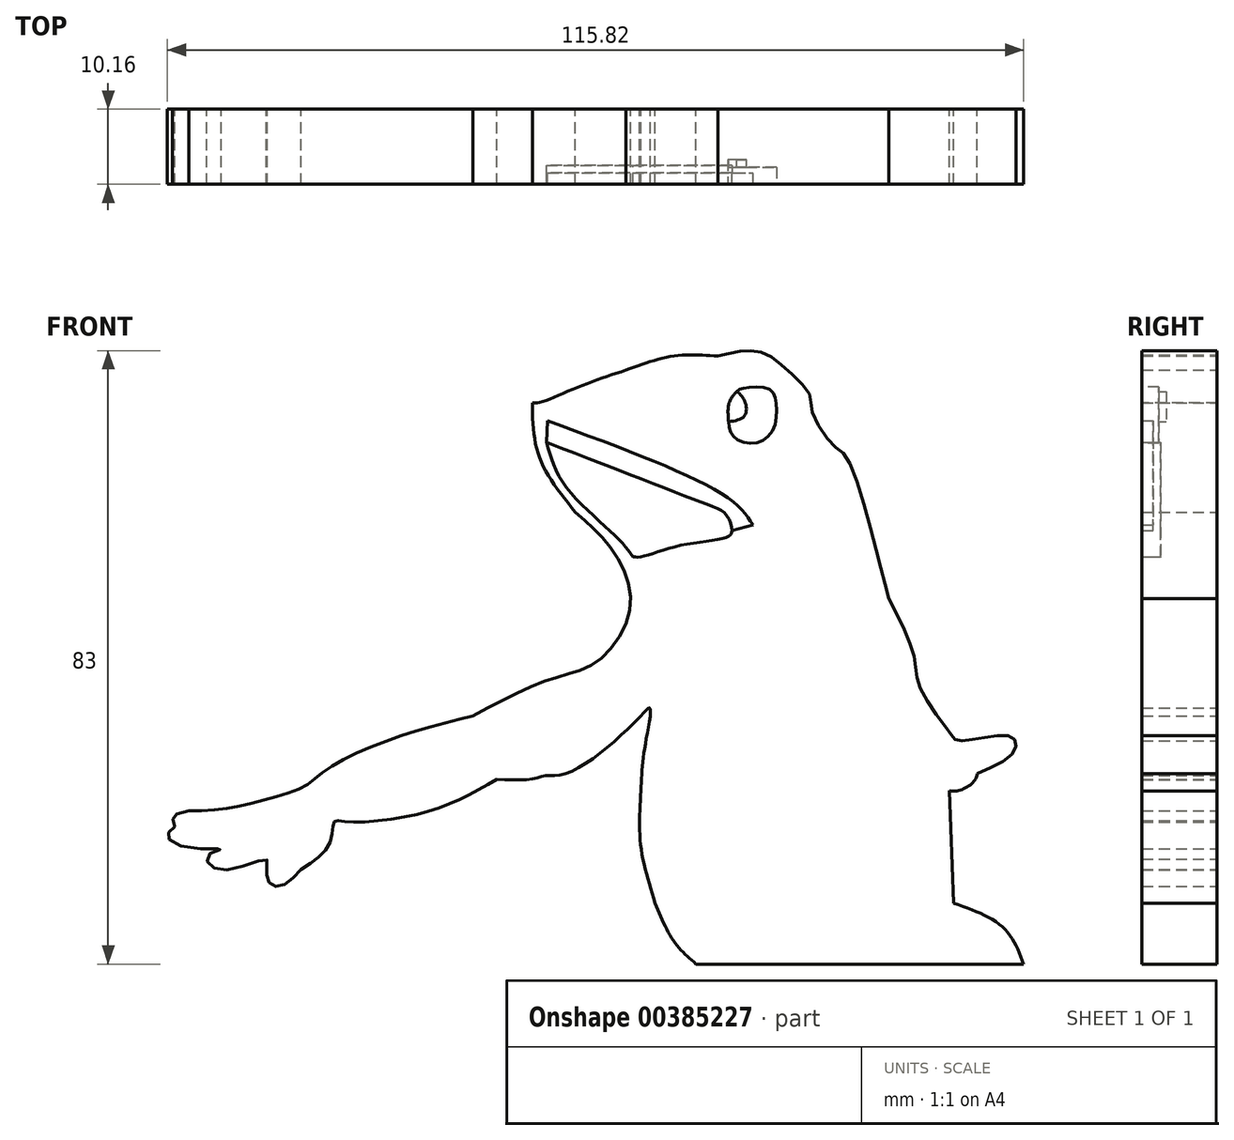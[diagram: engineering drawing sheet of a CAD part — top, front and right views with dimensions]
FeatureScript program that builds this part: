
annotation { "Feature Type Name" : "Feature", "Feature Type Description" : "" }
export const myFeature = defineFeature(function(context is Context, id is Id, definition is map)
    precondition{}
    {
        {
            var Q0;
            Q0=qCreatedBy(makeId("Front.planeOp"),FACE);
            var sketch = newSketch(context, id + "F0", { "sketchPlane" : qUnion([Q0])});
            skFitSpline(sketch, "E0", {"points": [v(-7.4, 26.5) * mm, v(-2.35, 21.3) * mm, v(0, 13.64) * mm, v(-4.52, 6.27) * mm, v(-11.02, 3.82) * mm, v(-21.28, -1.1) * mm], "startDerivative": vector(29, -25.3) * mm, "endDerivative": vector(-46.1, -24.95) * mm});
            skFitSpline(sketch, "E1", {"points": [v(-21.28, -1.1) * mm, v(-28.33, -2.93) * mm, v(-36.55, -5.9) * mm, v(-41.81, -8.85) * mm, v(-44.2, -10.67) * mm, v(-48.7, -12.2) * mm, v(-54.15, -13.54) * mm, v(-59.7, -13.92) * mm], "startDerivative": vector(-42.57, -10.25) * mm, "endDerivative": vector(-39.63, -0.97) * mm});
            skFitSpline(sketch, "E2", {"points": [v(-59.7, -13.92) * mm, v(-61.9, -14.78) * mm, v(-61.6, -16.03) * mm, v(-62.56, -17.08) * mm, v(-60.55, -18.7) * mm, v(-55.3, -19.09) * mm, v(-57.01, -19.85) * mm, v(-56.82, -21.28) * mm, v(-53.29, -21.67) * mm, v(-49.17, -20.52) * mm, v(-49.17, -21.57) * mm, v(-49.08, -23) * mm, v(-48.31, -24.06) * mm, v(-46.6, -23.77) * mm, v(-44.49, -21.86) * mm], "startDerivative": vector(-42.46, -7.69) * mm, "endDerivative": vector(24.54, 27.2) * mm});
            skFitSpline(sketch, "E3", {"points": [v(-44.49, -21.86) * mm, v(-40.57, -18.13) * mm, v(-40, -15.36) * mm, v(-38.66, -15.36) * mm, v(-30.72, -14.78) * mm, v(-23.55, -12.58) * mm, v(-18, -9.62) * mm], "startDerivative": vector(28.5, 18.95) * mm, "endDerivative": vector(28.54, 16.57) * mm});
            skFitSpline(sketch, "E4", {"points": [v(-18, -9.62) * mm, v(-13.32, -9.62) * mm, v(-11.37, -9.15) * mm, v(-9.27, -9.02) * mm, v(-4.35, -6.33) * mm, v(1.45, -1.1) * mm], "startDerivative": vector(24.57, -1.44) * mm, "endDerivative": vector(20.58, 20.22) * mm});
            skFitSpline(sketch, "E5", {"points": [v(1.45, -1.1) * mm, v(2.66, 0) * mm, v(2.27, -3.7) * mm, v(1.66, -7.93) * mm, v(1.45, -11.2) * mm], "startDerivative": vector(8.38, 10.25) * mm, "endDerivative": vector(-0.61, -12.7) * mm});
            skFitSpline(sketch, "E6", {"points": [v(1.45, -11.2) * mm, v(1.45, -18.68) * mm, v(3.4, -26.4) * mm], "startDerivative": vector(-0.94, -15.2) * mm, "endDerivative": vector(4.8, -15.2) * mm});
            skFitSpline(sketch, "E7", {"points": [v(3.4, -26.4) * mm, v(1.45, -30.92) * mm, v(-1.79, -34.64) * mm], "startDerivative": vector(-3.25, -9.45) * mm, "endDerivative": vector(-7.12, -7.03) * mm});
            skFitSpline(sketch, "E8", {"points": [v(3.4, -26.4) * mm, v(5.93, -31.58) * mm, v(8.9, -34.64) * mm], "startDerivative": vector(4.25, -10.45) * mm, "endDerivative": vector(6.84, -5.9) * mm});
            skFitSpline(sketch, "E9", {"points": [v(43.2, -11.2) * mm, v(43.75, -26.4) * mm], "startDerivative": vector(0.55, -15.2) * mm, "endDerivative": vector(0.55, -15.2) * mm});
            skFitSpline(sketch, "E10", {"points": [v(43.75, -26.4) * mm, v(50.47, -29.7) * mm, v(53.23, -34.64) * mm], "startDerivative": vector(14.34, -5) * mm, "endDerivative": vector(4.4, -11.64) * mm});
            skFitSpline(sketch, "E11", {"points": [v(43.2, -11.2) * mm, v(44.29, -11.2) * mm, v(46.35, -10.11) * mm, v(46.95, -8.91) * mm], "startDerivative": vector(3.44, -0.5) * mm, "endDerivative": vector(1.11, 3.96) * mm});
            skFitSpline(sketch, "E12", {"points": [v(46.95, -8.91) * mm, v(51.88, -5.91) * mm, v(51.88, -4.1) * mm, v(48.18, -3.93) * mm, v(44.21, -4.38) * mm, v(43.2, -3.3) * mm, v(39.16, 2.84) * mm, v(38.44, 6.8) * mm, v(35.01, 14.83) * mm], "startDerivative": vector(43.1, 18.83) * mm, "endDerivative": vector(-25.13, 49.69) * mm});
            skFitSpline(sketch, "E13", {"points": [v(23.2, 15.2) * mm, v(23.28, 3.65) * mm], "startDerivative": vector(0.1, -11.55) * mm, "endDerivative": vector(0.1, -11.55) * mm});
            skFitSpline(sketch, "E14", {"points": [v(23.28, 3.65) * mm, v(23.73, 2.55) * mm, v(25.33, 1.66) * mm], "startDerivative": vector(0.57, -2.65) * mm, "endDerivative": vector(3.42, -1.38) * mm});
            skFitSpline(sketch, "E15", {"points": [v(25.33, 1.66) * mm, v(25.12, 2.74) * mm], "startDerivative": vector(-0.21, 1.09) * mm, "endDerivative": vector(-0.21, 1.09) * mm});
            skFitSpline(sketch, "E16", {"points": [v(25.33, 1.66) * mm, v(26.38, -1.04) * mm, v(30.42, -5.41) * mm, v(31.88, -6.62) * mm], "startDerivative": vector(1.83, -8.12) * mm, "endDerivative": vector(4.88, -3.75) * mm});
            skFitSpline(sketch, "E17", {"points": [v(31.88, -6.62) * mm, v(32.96, -7.9) * mm, v(34.1, -9.43) * mm], "startDerivative": vector(2.21, -2.6) * mm, "endDerivative": vector(2.23, -3.01) * mm});
            skFitSpline(sketch, "E18", {"points": [v(33.45, -8.55) * mm, v(33.4, -10.6) * mm, v(32.88, -12.98) * mm, v(31.48, -16.79) * mm, v(30.7, -19.45) * mm], "startDerivative": vector(0.1, -9.6) * mm, "endDerivative": vector(-2.6, -10.02) * mm});
            skFitSpline(sketch, "E19", {"points": [v(30.7, -19.45) * mm, v(30.7, -20.82) * mm, v(32.66, -19.45) * mm, v(34.73, -14.35) * mm], "startDerivative": vector(-1.55, -8) * mm, "endDerivative": vector(3.26, 12.16) * mm});
            skFitSpline(sketch, "E20", {"points": [v(34.73, -14.35) * mm, v(35.77, -17.16) * mm, v(36.58, -17.27) * mm, v(39.77, -14.35) * mm, v(41.13, -10.9) * mm], "startDerivative": vector(3.62, -13.62) * mm, "endDerivative": vector(2.92, 11.75) * mm});
            skFitSpline(sketch, "E21", {"points": [v(41.13, -10.9) * mm, v(43.2, -11.2) * mm], "startDerivative": vector(2.06, -0.29) * mm, "endDerivative": vector(2.06, -0.29) * mm});
            skFitSpline(sketch, "E22", {"points": [v(-7.4, 26.5) * mm, v(-11.16, 31.63) * mm, v(-12.86, 36.1) * mm, v(-13.23, 41.3) * mm], "startDerivative": vector(-11.51, 14.32) * mm, "endDerivative": vector(-0.28, 16.38) * mm});
            skFitSpline(sketch, "E23", {"points": [v(-13.23, 41.3) * mm, v(-12.38, 41.3) * mm, v(-7.4, 43.27) * mm, v(-0.58, 45.72) * mm], "startDerivative": vector(4.42, -0.77) * mm, "endDerivative": vector(14.93, 4.95) * mm});
            skFitSpline(sketch, "E24", {"points": [v(35.01, 14.83) * mm, v(33.03, 22.23) * mm, v(29.3, 33.87) * mm, v(27.43, 35.59) * mm, v(24.6, 40.3) * mm, v(24.3, 42.3) * mm, v(21.31, 45.67) * mm, v(18.03, 48.06) * mm, v(15.04, 48.28) * mm, v(11.9, 47.6) * mm], "startDerivative": vector(-12.13, 44.2) * mm, "endDerivative": vector(-33.7, -8.68) * mm});
            skFitSpline(sketch, "E25", {"points": [v(11.9, 47.6) * mm, v(5.86, 47.6) * mm, v(-0.58, 45.72) * mm], "startDerivative": vector(-12.39, 0.9) * mm, "endDerivative": vector(-12.58, -4.63) * mm});
            skFitSpline(sketch, "E26", {"points": [v(15.41, 43.28) * mm, v(14.44, 42.83) * mm, v(13.4, 41.3) * mm, v(13.32, 38.72) * mm, v(13.92, 36.78) * mm, v(16.68, 35.81) * mm, v(19.3, 37.6) * mm, v(19.74, 41.3) * mm, v(18.77, 43.13) * mm, v(15.41, 43.28) * mm]});
            skFitSpline(sketch, "E27", {"points": [v(14.44, 42.83) * mm, v(15.49, 41.56) * mm, v(15.49, 39.55) * mm, v(13.32, 38.72) * mm], "startDerivative": vector(3.95, -3.5) * mm, "endDerivative": vector(-7.42, -1.12) * mm});
            skFitSpline(sketch, "E28", {"points": [v(-11.16, 38.87) * mm, v(13.25, 28.42) * mm, v(16.6, 24.76) * mm], "startDerivative": vector(43.3, -15.97) * mm, "endDerivative": vector(7.53, -11.69) * mm});
            skFitSpline(sketch, "E29", {"points": [v(0, 20.58) * mm, v(1.3, 20.43) * mm, v(6.46, 21.93) * mm, v(13.1, 23.12) * mm, v(13.77, 24.02) * mm, v(13.03, 26.1) * mm, v(10.11, 27.68) * mm, v(-11.31, 35.96) * mm], "startDerivative": vector(15.02, -4.32) * mm, "endDerivative": vector(-83.1, 32.46) * mm});
            skFitSpline(sketch, "E30", {"points": [v(-1.79, -34.64) * mm, v(8.9, -34.64) * mm, v(53.23, -34.64) * mm], "startDerivative": vector(26.93, 0) * mm, "endDerivative": vector(77.37, 0) * mm});
            skFitSpline(sketch, "E31", {"points": [v(23.2, 15.2) * mm, v(34.43, 16.95) * mm], "startDerivative": vector(11.24, 1.75) * mm, "endDerivative": vector(11.24, 1.75) * mm});
            skPoint(sketch, "E32.0.internal.orphan", {"position": v(37.9, -21.86) * mm});
            skPoint(sketch, "E32.1.internal.orphan", {"position": v(36.03, -26.4) * mm});
            skFitSpline(sketch, "E33", {"points": [v(-11.31, 35.96) * mm, v(-8.76, 30.04) * mm, v(-1.92, 23.2) * mm, v(0.38, 20.47) * mm], "startDerivative": vector(4.82, -17.39) * mm, "endDerivative": vector(7.13, -9.8) * mm});
            skFitSpline(sketch, "E34", {"points": [v(13.77, 24.02) * mm, v(16.6, 24.76) * mm], "startDerivative": vector(2.84, 0.75) * mm, "endDerivative": vector(2.84, 0.75) * mm});
            skFitSpline(sketch, "E35", {"points": [v(-11.31, 35.96) * mm, v(-11.16, 38.87) * mm], "startDerivative": vector(0.15, 2.91) * mm, "endDerivative": vector(0.15, 2.91) * mm});
            skSolve(sketch);
        }
        {
            var Q0;
            Q0=makeQuery(id+"F0.imprint","IMPRINT",FACE,{"disambiguationData":[TD([[makeQuery(id+"F0.imprint","IMPRINT",EDGE,{"derivedFrom":sQuery(id+"F0.wireOp",EDGE,"E0")}),1.0]])]});
            extrude(context, id + "F1", {"entities" : qUnion([Q0]), "depth" : 10.16 * mm});
        }
        {
            var Q0;
            {var subQ0=sQuery(id+"F0.wireOp",EDGE,"E27");Q0=makeQuery(id+"F0.imprint","IMPRINT",FACE,{"disambiguationData":[TD([[makeQuery(id+"F0.imprint","IMPRINT",EDGE,{"derivedFrom":subQ0}),1.0]])]});}
            extrude(context, id + "F2", {"entities" : qUnion([Q0]), "operationType" : NewBodyOperationType.ADD, "depth" : 7.87 * mm});
        }
        {
            var Q0;
            {var subQ0=sQuery(id+"F0.wireOp",EDGE,"E27");Q0=makeQuery(id+"F0.imprint","IMPRINT",FACE,{"disambiguationData":[TD([[makeQuery(id+"F0.imprint","IMPRINT",EDGE,{"derivedFrom":subQ0}),-1.0]])]});}
            extrude(context, id + "F3", {"entities" : qUnion([Q0]), "operationType" : NewBodyOperationType.ADD, "depth" : 6.86 * mm});
        }
        {
            var Q0;
            {var subQ0=sQuery(id+"F0.wireOp",EDGE,"E29");var subQ1=makeQuery(id+"F0.imprint","INTERSECT",VERTEX,{"derivedFrom":[subQ0,sQuery(id+"F0.wireOp",EDGE,"E34")]});Q0=makeQuery(id+"F0.imprint","IMPRINT",FACE,{"disambiguationData":[TD([[makeQuery(id+"F0.imprint","IMPRINT",EDGE,{"disambiguationData":[TD([[subQ1,1.0]])],"derivedFrom":subQ0}),1.0]])]});}
            extrude(context, id + "F4", {"entities" : qUnion([Q0]), "operationType" : NewBodyOperationType.ADD, "depth" : 7.62 * mm});
        }
        {
            var Q0;
            Q0=makeQuery(id+"F0.imprint","IMPRINT",FACE,{"disambiguationData":[TD([[makeQuery(id+"F0.imprint","IMPRINT",EDGE,{"derivedFrom":sQuery(id+"F0.wireOp",EDGE,"E28")}),-1.0]])]});
            extrude(context, id + "F5", {"entities" : qUnion([Q0]), "operationType" : NewBodyOperationType.ADD, "depth" : 8.64 * mm});
        }
    });
